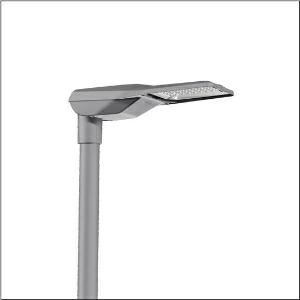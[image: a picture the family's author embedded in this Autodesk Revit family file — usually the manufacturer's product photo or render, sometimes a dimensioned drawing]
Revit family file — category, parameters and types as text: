
# Revit family: streetlight_sl_21_iq_mini___st0_8a_5xe2c41g08jb_e7d2
name_source: partatom
category: Lighting Fixtures
units: mm (PartAtom-declared; Revit-internal decimal feet)

## family parameters
Cut with Voids When Loaded = No
Host = Face
Light Source = No
Part Type = Normal
Room Calculation Point = No
Round Connector Dimension = Use Diameter
Shared = No

## types (1)
- --- (1 x LED, 11290 lm, 71.6 W, 4000K)
    Apparent Load = 72 VA
    CIE Flux Codes = 41 75 97 100 100
    Color Rendering = 70
    Color Temperature = 4000K
    Default Elevation = 1800 mm
    Description = Streetlight SL 21 iQ mini, mast luminaire, primary light control with lens, of PMMA, primary optical cover: cover, of toughened safety glass, transparent, light distribution: ST0.8a, light emission: direct distribution, primary light characteristic: asymmetric, installation type: post-top, side-entry, LED, High Power LED, rated luminous flux: 11.290lm, luminous efficacy: 158lm/W, light colour: 740, colour temperature: 4000K, control: Street-Remote, Auto-Match, Temp-Guard, Lumen-Switch, Night-Set, Smart-Wire, Light-Fading, Desk-Remote (wireless, voltage-free reading and setting of iQ features in the workshop via application-optimized NFC function/RFID function), optimised constant luminous flux control (CLO 2.0), pre-setting: linear dimming characteristic, mains connection: 220..240V, AC, 50/60Hz, start of lifetime: 72W, end of service life: 75W, reduction: 33W, luminaire housing, of diecast aluminium, powder-coated, Siteco® metallic grey (DB 702S), corrosivity category C5 mid according to DIN EN ISO 12944, please order mast flange separately, inclination adjustable: 0°, 5°, 10°, 15°, sealing non-destructively replaceable, multi-level sealing system, length: 628mm, width: 235mm, height: 110mm, mast flange for spigot size: 42mm (side-entry): 5XC10008XM4, 60/48mm (side-entry/post-top): 5XC10108XM2, 76/60mm (side-entry/post-top): 5XC10108XM1, protection rating (complete): IP66, insulation class (complete): insulation class II (safety insulation), certification: CE, ENEC, ENEC+, VDE, impact resistance: IK09, permissible operating ambient temperature for outdoor applications: -40..+50°C, standard-compliant lighting for roads and squares, packaging unit: 1 piece

Light Distribution: ST0.8a
    Height = 110 mm
    Lamp = 1 x LED
    Lamp Light Flux = 11290 lm
    Lamp Power = 71.6 W
    Lamp count = 1
    Length = 625 mm
    Luminous efficacy = 158 lm/W
    Manufacturer = Siteco
    ModVariant = No
    Model = 5XE2C41G08JB
    Number of Poles = 1
    OnlyDefault = Yes
    Power Factor = 1
    Product Name = Streetlight SL 21 iQ mini | ST0.8a
    Product group = mast luminaire | pylon top
    ProductGroupID = 6100
    Protection Class = Protection class II
    Protection Degree = IP 66
    RLX_Detail_Level = 1
    RLX_Emergency_Light_Flux = 0 lm
    RLX_Emergency_Type = 0
    RLX_Emergency_Type_DB = No
    RlxData = <blob elided: 93709 chars, md5=19c96349>
    Socket = socket
    Standby Power = 0 W
    System Light Flux = 11290 lm
    System Power = 72 W
    Type Comments = factory setting: luminous flux: 100 % | dim-lin: 254 | 746 mA
    Type Image = l_1003519.jpg
    URL = http://relux.com
    VarID = @adj_139807
    Voltage = 0 V
    Weight = 0.00 kg
    Width = 234 mm

## geometry (parser evidence)
native form markers: Blend x4, Sweep x11
no freeform markers — native parametric forms only
